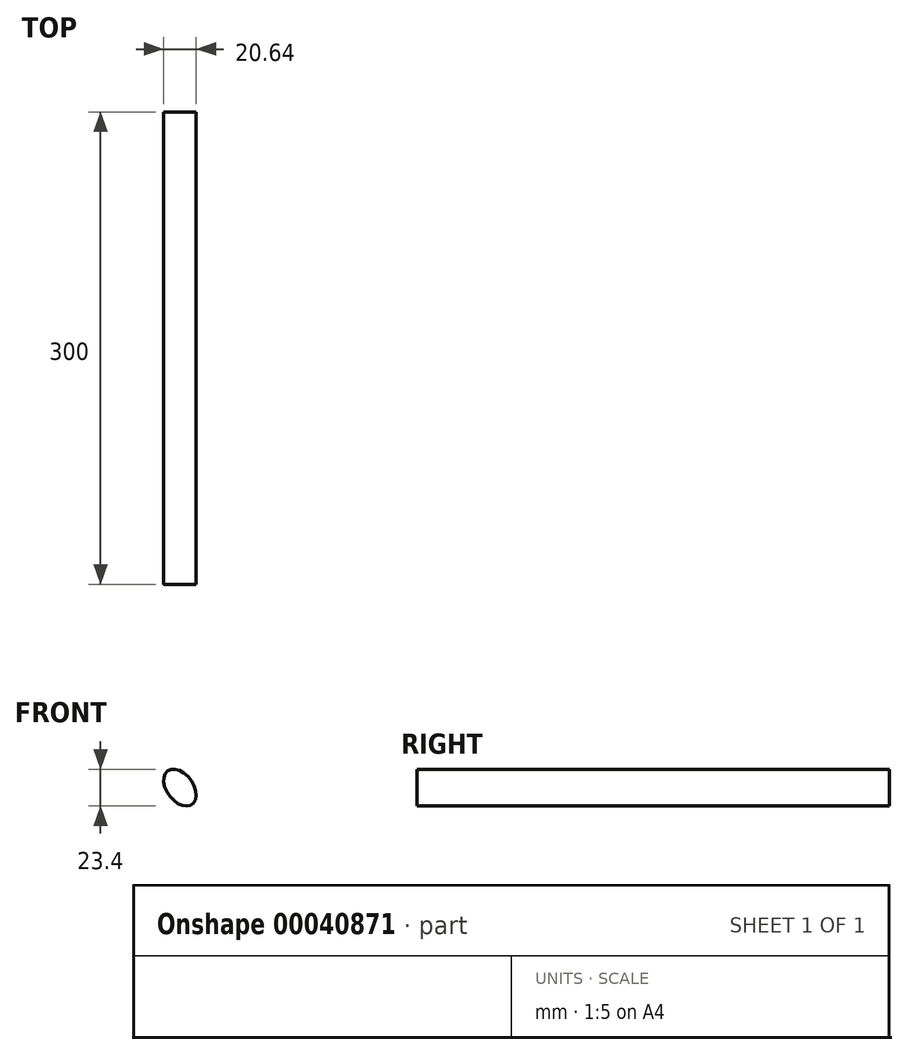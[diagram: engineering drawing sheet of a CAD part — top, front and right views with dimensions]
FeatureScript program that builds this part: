
annotation { "Feature Type Name" : "Feature", "Feature Type Description" : "" }
export const myFeature = defineFeature(function(context is Context, id is Id, definition is map)
    precondition{}
    {
        {
            var Q0;
            Q0=qCreatedBy(makeId("Front.planeOp"),FACE);
            var sketch = newSketch(context, id + "F0", { "sketchPlane" : qUnion([Q0])});
            skEllipse(sketch, "E0.3.0", {"center": v(0, 0) * mm, "majorRadius": 13.13 * mm, "minorRadius": 8.42 * mm, "majorAxis": v(-0.6, 0.8)});
            skSolve(sketch);
        }
        {
            var Q0;
            Q0=makeQuery(id+"F0.imprint","IMPRINT",FACE,{"disambiguationData":[TD([[makeQuery(id+"F0.imprint","IMPRINT",EDGE,{"derivedFrom":sQuery(id+"F0.wireOp",EDGE,"E0.3.0")}),1.0]])]});
            extrude(context, id + "F1", {"entities" : qUnion([Q0]), "depth" : 300 * mm});
        }
    });
